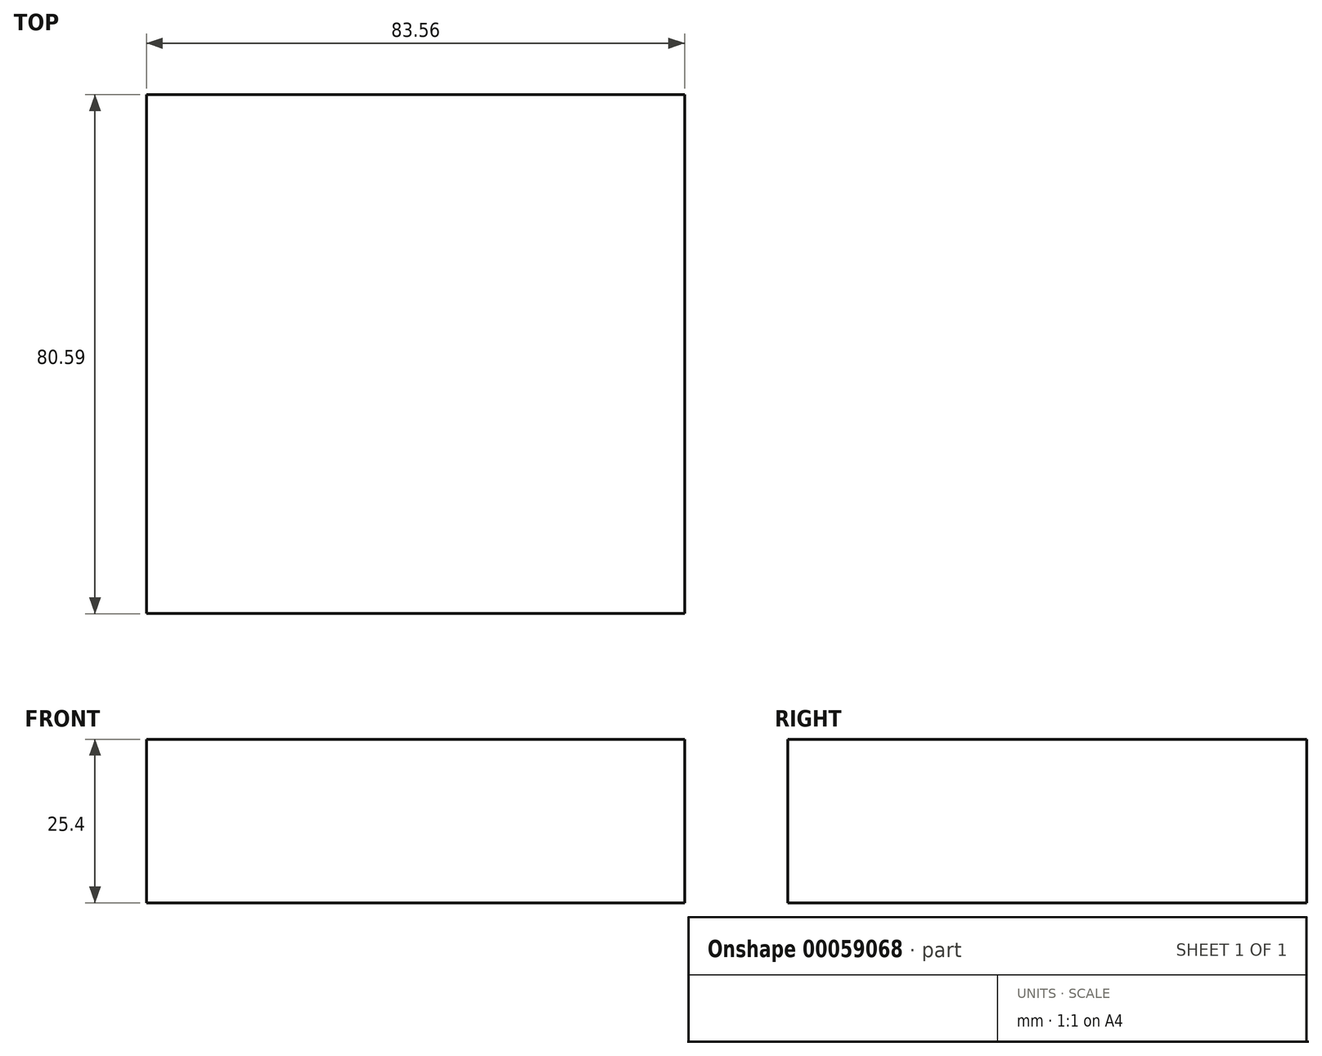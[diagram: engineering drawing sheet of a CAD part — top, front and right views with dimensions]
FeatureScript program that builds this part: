
annotation { "Feature Type Name" : "Feature", "Feature Type Description" : "" }
export const myFeature = defineFeature(function(context is Context, id is Id, definition is map)
    precondition{}
    {
        {
            var Q0;
            Q0=qCreatedBy(makeId("Top.planeOp"),FACE);
            var sketch = newSketch(context, id + "F0", { "sketchPlane" : qUnion([Q0])});
            skLineSegment(sketch, "E0.bottom", {"start": v(-58.38, -49.52) * mm, "end": v(25.18, -49.52) * mm});
            skLineSegment(sketch, "E0.top", {"start": v(-58.38, 31.07) * mm, "end": v(25.18, 31.07) * mm});
            skLineSegment(sketch, "E0.left", {"start": v(-58.38, -49.52) * mm, "end": v(-58.38, 31.07) * mm});
            skLineSegment(sketch, "E0.right", {"start": v(25.18, -49.52) * mm, "end": v(25.18, 31.07) * mm});
            skSolve(sketch);
        }
        {
            var Q0;
            Q0 = qSketchRegion(id + "F0", true);
            extrude(context, id + "F1", {"entities" : qUnion([Q0]), "depth" : 25.4 * mm});
        }
    });
